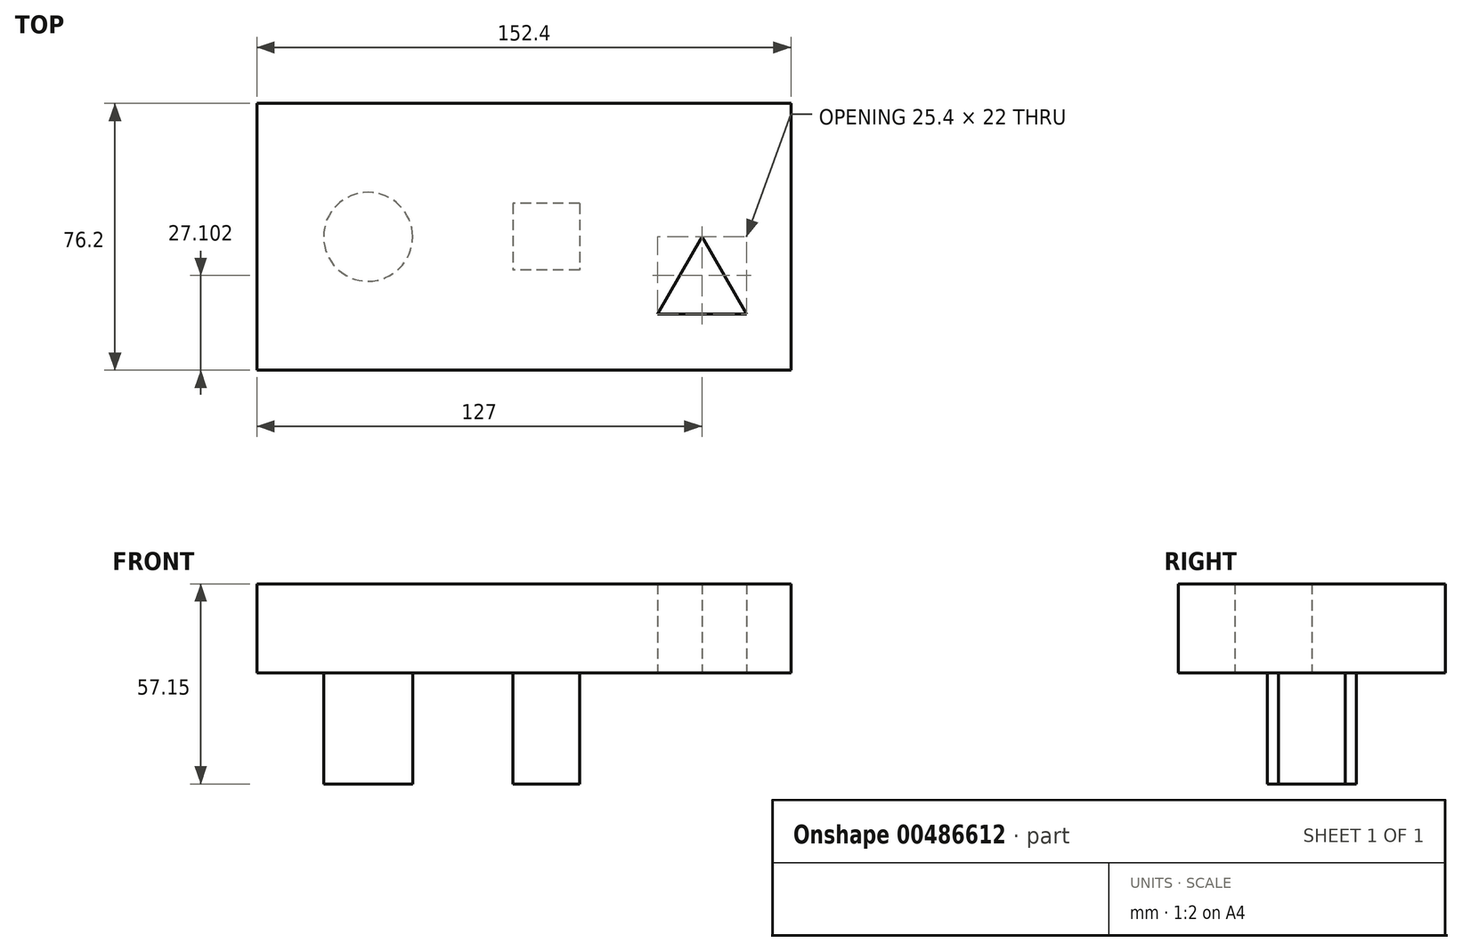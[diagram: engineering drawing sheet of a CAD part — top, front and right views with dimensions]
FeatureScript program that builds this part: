
annotation { "Feature Type Name" : "Feature", "Feature Type Description" : "" }
export const myFeature = defineFeature(function(context is Context, id is Id, definition is map)
    precondition{}
    {
        {
            var Q0;
            Q0=qCreatedBy(makeId("Top.planeOp"),FACE);
            var sketch = newSketch(context, id + "F0", { "sketchPlane" : qUnion([Q0])});
            skLineSegment(sketch, "E0.bottom", {"start": v(38.1, 38.1) * mm, "end": v(-114.3, 38.1) * mm});
            skLineSegment(sketch, "E0.top", {"start": v(38.1, -38.1) * mm, "end": v(-114.3, -38.1) * mm});
            skLineSegment(sketch, "E0.left", {"start": v(38.1, 38.1) * mm, "end": v(38.1, -38.1) * mm});
            skLineSegment(sketch, "E0.right", {"start": v(-114.3, 38.1) * mm, "end": v(-114.3, -38.1) * mm});
            skPoint(sketch, "E0.middle", {"position": v(-38.1, 0) * mm});
            skLineSegment(sketch, "E1", {"start": v(0, 0) * mm, "end": v(-31.75, 0) * mm});
            skLineSegment(sketch, "E2.bottom", {"start": v(-22.22, 9.53) * mm, "end": v(-41.27, 9.53) * mm});
            skLineSegment(sketch, "E2.top", {"start": v(-22.22, -9.53) * mm, "end": v(-41.28, -9.52) * mm});
            skLineSegment(sketch, "E2.left", {"start": v(-22.22, 9.53) * mm, "end": v(-22.22, -9.53) * mm});
            skLineSegment(sketch, "E2.right", {"start": v(-41.27, 9.53) * mm, "end": v(-41.27, -9.52) * mm});
            skPoint(sketch, "E2.middle", {"position": v(-31.75, 0) * mm});
            skLineSegment(sketch, "E3", {"start": v(-31.75, 0) * mm, "end": v(-82.55, 0) * mm});
            skCircle(sketch, "E4", {"center": v(-82.55, 0) * mm, "radius": 12.7 * mm});
            skLineSegment(sketch, "E5", {"start": v(12.7, 0) * mm, "end": v(0, -22) * mm});
            skLineSegment(sketch, "E6", {"start": v(0, -22) * mm, "end": v(25.4, -22) * mm});
            skLineSegment(sketch, "E7", {"start": v(25.4, -22) * mm, "end": v(12.7, 0) * mm});
            skLineSegment(sketch, "E8", {"start": v(0, 0) * mm, "end": v(12.7, 0) * mm});
            skSolve(sketch);
        }
        {
            var Q0;
            Q0=makeQuery(id+"F0.imprint","IMPRINT",FACE,{"disambiguationData":[TD([[makeQuery(id+"F0.imprint","IMPRINT",EDGE,{"derivedFrom":sQuery(id+"F0.wireOp",EDGE,"E0.bottom")}),1.0]])]});
            var Q1;
            Q1=makeQuery(id+"F0.imprint","IMPRINT",FACE,{"disambiguationData":[TD([[makeQuery(id+"F0.imprint","IMPRINT",EDGE,{"derivedFrom":sQuery(id+"F0.wireOp",EDGE,"E4")}),1.0]])]});
            var Q2;
            {var subQ1=sQuery(id+"F0.wireOp",EDGE,"E2.bottom");Q2=makeQuery(id+"F0.imprint","IMPRINT",FACE,{"disambiguationData":[TD([[makeQuery(id+"F0.imprint","IMPRINT",EDGE,{"derivedFrom":subQ1}),1.0]])]});}
            var Q3;
            {var subQ1=sQuery(id+"F0.wireOp",EDGE,"E2.top");Q3=makeQuery(id+"F0.imprint","IMPRINT",FACE,{"disambiguationData":[TD([[makeQuery(id+"F0.imprint","IMPRINT",EDGE,{"derivedFrom":subQ1}),-1.0]])]});}
            extrude(context, id + "F1", {"entities" : qUnion([Q0, Q1, Q2, Q3]), "depth" : 25.4 * mm});
        }
        {
            var Q0;
            Q0=makeQuery(id+"F0.imprint","IMPRINT",FACE,{"disambiguationData":[TD([[makeQuery(id+"F0.imprint","IMPRINT",EDGE,{"derivedFrom":sQuery(id+"F0.wireOp",EDGE,"E4")}),1.0]])]});
            var Q1;
            {var subQ1=sQuery(id+"F0.wireOp",EDGE,"E2.bottom");Q1=makeQuery(id+"F0.imprint","IMPRINT",FACE,{"disambiguationData":[TD([[makeQuery(id+"F0.imprint","IMPRINT",EDGE,{"derivedFrom":subQ1}),1.0]])]});}
            var Q2;
            {var subQ1=sQuery(id+"F0.wireOp",EDGE,"E2.top");Q2=makeQuery(id+"F0.imprint","IMPRINT",FACE,{"disambiguationData":[TD([[makeQuery(id+"F0.imprint","IMPRINT",EDGE,{"derivedFrom":subQ1}),-1.0]])]});}
            extrude(context, id + "F2", {"entities" : qUnion([Q0, Q1, Q2]), "operationType" : NewBodyOperationType.ADD, "oppositeDirection" : true, "depth" : 31.75 * mm});
        }
    });
